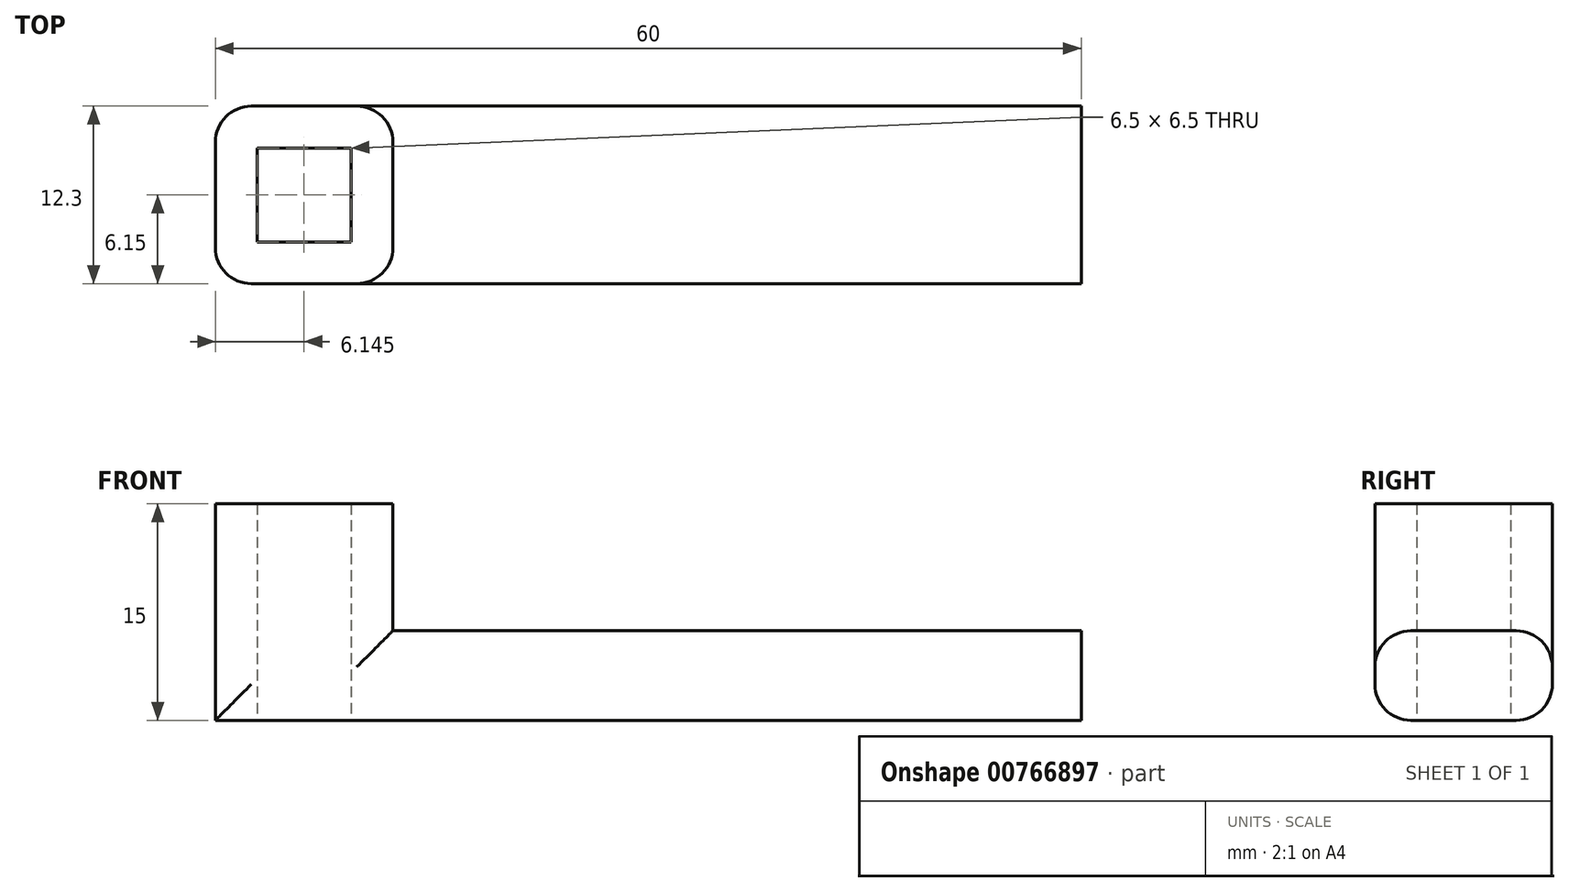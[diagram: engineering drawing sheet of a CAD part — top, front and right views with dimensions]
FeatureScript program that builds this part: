
annotation { "Feature Type Name" : "Feature", "Feature Type Description" : "" }
export const myFeature = defineFeature(function(context is Context, id is Id, definition is map)
    precondition{}
    {
        {
            var Q0;
            Q0=qCreatedBy(makeId("Top.planeOp"),FACE);
            var sketch = newSketch(context, id + "F0", { "sketchPlane" : qUnion([Q0])});
            skLineSegment(sketch, "E0.bottom", {"start": v(-33.63, -24.03) * mm, "end": v(26.37, -24.03) * mm});
            skLineSegment(sketch, "E0.top", {"start": v(-33.63, -36.33) * mm, "end": v(26.37, -36.33) * mm});
            skLineSegment(sketch, "E0.left", {"start": v(-33.63, -24.03) * mm, "end": v(-33.63, -36.33) * mm});
            skLineSegment(sketch, "E0.right", {"start": v(26.37, -24.03) * mm, "end": v(26.37, -36.33) * mm});
            skLineSegment(sketch, "E1.bottom", {"start": v(-30.73, -26.93) * mm, "end": v(-24.23, -26.93) * mm});
            skLineSegment(sketch, "E1.top", {"start": v(-30.73, -33.43) * mm, "end": v(-24.23, -33.43) * mm});
            skLineSegment(sketch, "E1.left", {"start": v(-30.73, -26.93) * mm, "end": v(-30.73, -33.43) * mm});
            skLineSegment(sketch, "E1.right", {"start": v(-24.23, -26.93) * mm, "end": v(-24.23, -33.43) * mm});
            skLineSegment(sketch, "E2", {"start": v(-21.33, -24.03) * mm, "end": v(-21.33, -36.33) * mm});
            skSolve(sketch);
        }
        {
            var Q0;
            {var subQ0=sQuery(id+"F0.wireOp",EDGE,"E0.right");Q0=makeQuery(id+"F0.imprint","IMPRINT",FACE,{"disambiguationData":[TD([[makeQuery(id+"F0.imprint","IMPRINT",EDGE,{"derivedFrom":subQ0}),-1.0]])]});}
            extrude(context, id + "F1", {"entities" : qUnion([Q0]), "depth" : 6.2 * mm, "offsetDistance" : 25 * mm});
        }
        {
            var Q0;
            {var subQ0=sQuery(id+"F0.wireOp",EDGE,"E0.left");Q0=makeQuery(id+"F0.imprint","IMPRINT",FACE,{"disambiguationData":[TD([[makeQuery(id+"F0.imprint","IMPRINT",EDGE,{"derivedFrom":subQ0}),1.0]])]});}
            extrude(context, id + "F2", {"entities" : qUnion([Q0]), "operationType" : NewBodyOperationType.ADD, "depth" : 15 * mm, "offsetDistance" : 25 * mm});
        }
        {
            var Q0;
            Q0=makeQuery(id+"F1.opExtrude","CAP_EDGE",EDGE,{"disambiguationData":[OSD([sQuery(id+"F0.wireOp",EDGE,"E0.top")])],"isStart":false});
            var Q1;
            Q1=makeQuery(id+"F1.opExtrude","CAP_EDGE",EDGE,{"disambiguationData":[OSD([sQuery(id+"F0.wireOp",EDGE,"E0.bottom")])],"isStart":false});
            var Q2;
            {var subQ0=sQuery(id+"F0.wireOp",EDGE,"E0.bottom");Q2=makeQuery(id+"F2.boolean.opBoolean","MERGE",EDGE,{"derivedFrom":[makeQuery(id+"F1.opExtrude","CAP_EDGE",EDGE,{"disambiguationData":[OSD([subQ0])],"isStart":true}),makeQuery(id+"F2.opExtrude","CAP_EDGE",EDGE,{"disambiguationData":[OSD([subQ0])],"isStart":true})]});}
            var Q3;
            {var subQ0=sQuery(id+"F0.wireOp",EDGE,"E0.top");Q3=makeQuery(id+"F2.boolean.opBoolean","MERGE",EDGE,{"derivedFrom":[makeQuery(id+"F1.opExtrude","CAP_EDGE",EDGE,{"disambiguationData":[OSD([subQ0])],"isStart":true}),makeQuery(id+"F2.opExtrude","CAP_EDGE",EDGE,{"disambiguationData":[OSD([subQ0])],"isStart":true})]});}
            var Q4;
            Q4=makeQuery(id+"F2.opExtrude","SWEPT_EDGE",EDGE,{"disambiguationData":[OSD([sQuery(id+"F0.wireOp",EDGE,"E0.top"),sQuery(id+"F0.wireOp",EDGE,"E0.left")])]});
            var Q5;
            Q5=makeQuery(id+"F2.opExtrude","SWEPT_EDGE",EDGE,{"disambiguationData":[OSD([sQuery(id+"F0.wireOp",EDGE,"E0.top"),sQuery(id+"F0.wireOp",EDGE,"E2")])]});
            var Q6;
            Q6=makeQuery(id+"F2.opExtrude","SWEPT_EDGE",EDGE,{"disambiguationData":[OSD([sQuery(id+"F0.wireOp",EDGE,"E0.bottom"),sQuery(id+"F0.wireOp",EDGE,"E2")])]});
            var Q7;
            Q7=makeQuery(id+"F2.opExtrude","SWEPT_EDGE",EDGE,{"disambiguationData":[OSD([sQuery(id+"F0.wireOp",EDGE,"E0.bottom"),sQuery(id+"F0.wireOp",EDGE,"E0.left")])]});
            fillet(context, id + "F3", {"entities" : qUnion([Q0, Q1, Q2, Q3, Q4, Q5, Q6, Q7]), "radius" : 2.5 * mm, "tangentPropagation" : true, "allowEdgeOverflow" : false});
        }
    });
